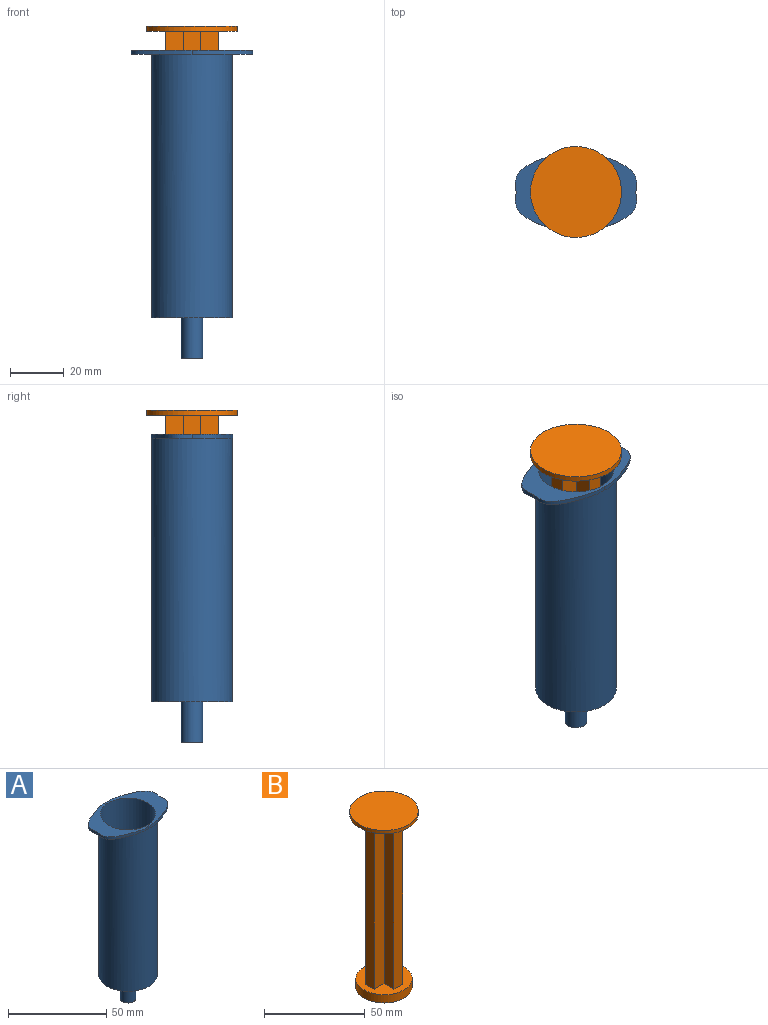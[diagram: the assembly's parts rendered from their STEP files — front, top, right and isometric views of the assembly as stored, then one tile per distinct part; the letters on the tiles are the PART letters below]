
ASSEMBLY  parts=2 mates=1
PART A: 14 faces, bbox 46.4x31.2x115 mm
  f0: cylinder r=15mm len=98.5mm, axis (0,0,-1), area 9283.4mm2, adj f3,f10,f13
  f1: cylinder r=2.5mm len=17mm, axis (0,0,-1), area 267mm2, adj f2,f7
  f2: plane 28x28mm, normal (0,0,1), area 596.1mm2, adj f1,f4
  f3: plane 30x30mm, normal (0,0,-1), area 656.6mm2, adj f0,f6
  f4: cylinder r=14mm len=98mm, axis (0,0,-1), area 8620.5mm2, adj f2,f5
  f5: plane 46.36x31.19mm, normal (0,0,1), area 495.1mm2, adj f4,f8,f9,f11,f12
  f6: cylinder r=4mm len=15mm, axis (0,0,1), area 377mm2, adj f3,f7
  f7: plane 8x8mm, normal (0,0,-1), area 30.6mm2, adj f1,f6
  f8: extruded ~22.64x15.22mm, area 46.2mm2, adj f5,f9,f10,f11
  f9: extruded ~22.64x15.22mm, area 46.2mm2, adj f5,f8,f10,f12
  f10: plane 31.19x23.18mm, normal (0,0,-1), area 202mm2, adj f0,f8,f9
  f11: extruded ~22.64x15.22mm, area 46.2mm2, adj f5,f8,f12,f13
  f12: extruded ~22.64x15.22mm, area 46.2mm2, adj f5,f9,f11,f13
  f13: plane 31.19x23.18mm, normal (0,0,-1), area 202mm2, adj f0,f11,f12
PART B: 18 faces, bbox 34x34x107 mm
  f0: cylinder r=14mm len=28mm, axis (0,0,1), area 439.8mm2, adj f1,f2
  f1: plane 28x28mm, normal (0,0,-1), area 615.8mm2, adj f0
  f2: plane 28x28mm, normal (0,0,1), area 411.8mm2, adj f0,f3,f4,f5,f6,f7,f8,f9
  f3: plane 100x7mm, normal (0,1,0), area 700mm2, adj f2,f4,f14,f15
  f4: plane 100x7mm, normal (1,0,0), area 700mm2, adj f2,f3,f5,f15
  f5: plane 100x6mm, normal (0,1,0), area 600mm2, adj f2,f4,f6,f15
  f6: plane 100x7mm, normal (-1,0,0), area 700mm2, adj f2,f5,f7,f15
  f7: plane 100x7mm, normal (0,1,0), area 700mm2, adj f2,f6,f8,f15
  f8: plane 100x6mm, normal (-1,0,0), area 600mm2, adj f2,f7,f9,f15
  f9: plane 100x7mm, normal (0,-1,0), area 700mm2, adj f2,f8,f10,f15
  f10: plane 100x7mm, normal (-1,0,0), area 700mm2, adj f2,f9,f11,f15
  f11: plane 100x6mm, normal (0,-1,0), area 600mm2, adj f2,f10,f12,f15
  f12: plane 100x7mm, normal (1,0,0), area 700mm2, adj f2,f11,f13,f15
  f13: plane 100x7mm, normal (0,-1,0), area 700mm2, adj f2,f12,f14,f15
  f14: plane 100x6mm, normal (1,0,0), area 600mm2, adj f2,f3,f13,f15
  f15: plane 34x34mm, normal (0,0,-1), area 703.9mm2, adj f3,f4,f5,f6,f7,f8,f9,f10
  f16: cylinder r=17mm len=34mm, axis (0,0,-1), area 213.6mm2, adj f15,f17
  f17: plane 34x34mm, normal (0,0,1), area 907.9mm2, adj f16
PLACE A t=(26.45,16.09,37)mm
PLACE B t=(26.45,16.09,44)mm
MATE slider B.f0 <-> A.f4  axis (0,0,-1) through (26.45,16.09,39)mm
